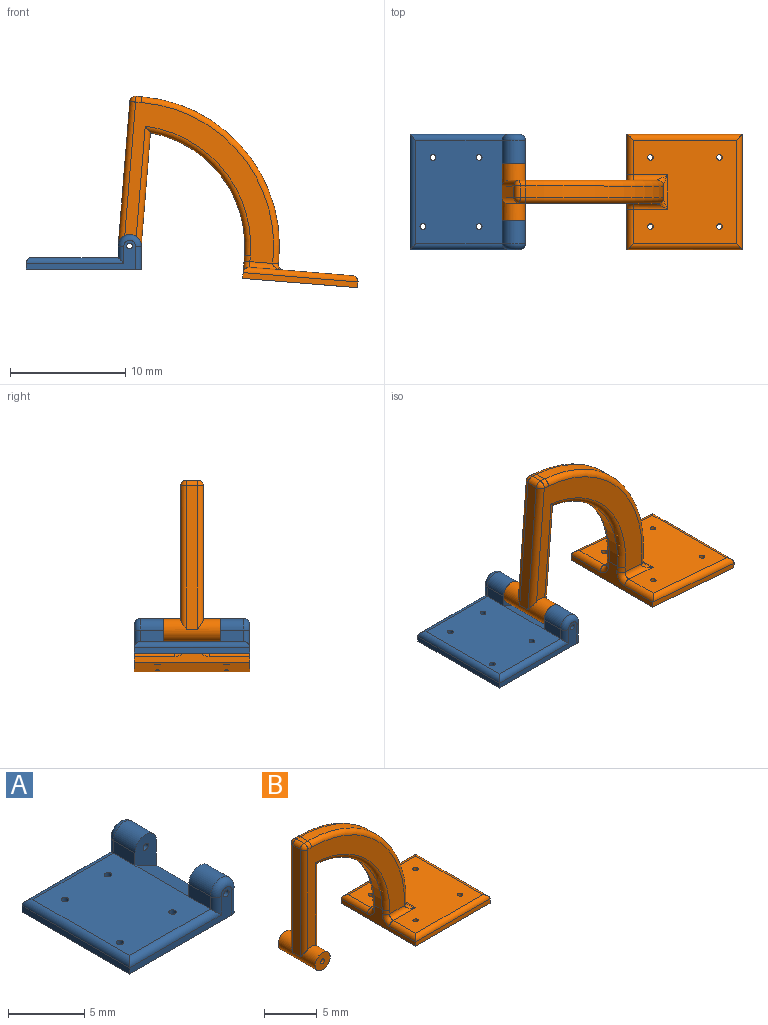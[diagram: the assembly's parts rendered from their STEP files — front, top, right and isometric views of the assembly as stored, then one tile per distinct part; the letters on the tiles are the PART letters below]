
ASSEMBLY  parts=2 mates=1
PART A: 29 faces, bbox 10.1x10x3.1 mm
  f0: plane 2x2mm, normal (1,0,0), area 4mm2, adj f2,f9,f18,f28
  f1: plane 2x1mm, normal (-1,0,0), area 2mm2, adj f5,f7,f19,f23
  f2: cylinder r=1mm len=2mm, axis (0,1,0), area 6.3mm2, adj f0,f6,f18,f27
  f3: cylinder r=0.25mm len=2.5mm, axis (0,-1,0), area 3.9mm2, adj f11,f18
  f4: plane 2x2mm, normal (1,0,0), area 4mm2, adj f5,f9,f19,f25
  f5: cylinder r=1mm len=2mm, axis (0,1,0), area 6.3mm2, adj f1,f4,f19,f24
  f6: plane 2x1mm, normal (-1,0,0), area 2mm2, adj f2,f7,f18,f26
  f7: plane 9x7.5mm, normal (0,0,1), area 66.7mm2, adj f1,f6,f12,f13,f14,f15,f17,f20
  f8: plane 10x0.5mm, normal (-1,0,0), area 5mm2, adj f9,f10,f11,f22
  f9: plane 10x10mm, normal (0,0,-1), area 99.1mm2, adj f0,f4,f8,f10,f11,f12,f13,f14
  f10: plane 9.5x2.5mm, normal (0,-1,0), area 6.4mm2, adj f8,f9,f16,f20,f23,f24,f25
  f11: plane 9.5x2.5mm, normal (0,1,0), area 6.4mm2, adj f3,f8,f9,f21,f26,f27,f28
  f12: cylinder r=0.25mm len=1mm, axis (0,0,1), area 1.6mm2, adj f7,f9
  f13: cylinder r=0.25mm len=1mm, axis (0,0,1), area 1.6mm2, adj f7,f9
  f14: cylinder r=0.25mm len=1mm, axis (0,0,1), area 1.6mm2, adj f7,f9
  f15: cylinder r=0.25mm len=1mm, axis (0,0,1), area 1.6mm2, adj f7,f9
  f16: cylinder r=0.25mm len=2.5mm, axis (0,-1,0), area 3.9mm2, adj f10,f19
  f17: plane 5x2mm, normal (0.45,0,0.89), area 11.2mm2, adj f7,f9,f18,f19
  f18: plane 3x2mm, normal (0,-1,0), area 4.4mm2, adj f0,f2,f3,f6,f17
  f19: plane 3x2mm, normal (0,1,0), area 4.4mm2, adj f1,f4,f5,f16,f17
  f20: cylinder r=0.5mm len=8.5mm, axis (1,0,0), area 6.3mm2, adj f7,f10,f22,f23
  f21: cylinder r=0.5mm len=8.5mm, axis (-1,0,0), area 6.3mm2, adj f7,f11,f22,f26
  f22: cylinder r=0.5mm len=10mm, axis (0,-1,0), area 7.6mm2, adj f7,f8,f20,f21
  f23: cylinder r=0.5mm len=1.5mm, axis (0,0,1), area 0.9mm2, adj f1,f10,f20,f24
  f24: torus R=0.5mm, axis (0,-1,0), area 2mm2, adj f5,f10,f23,f25
  f25: cylinder r=0.5mm len=2mm, axis (0,0,-1), area 1.6mm2, adj f4,f9,f10,f24
  f26: cylinder r=0.5mm len=1.5mm, axis (0,0,-1), area 0.9mm2, adj f6,f11,f21,f27
  f27: torus R=0.5mm, axis (0,-1,0), area 2mm2, adj f2,f11,f26,f28
  f28: cylinder r=0.5mm len=2mm, axis (0,0,1), area 1.6mm2, adj f0,f9,f11,f27
PART B: 50 faces, bbox 21x10x16.1 mm
  f0: plane 9x9mm, normal (0,0,1), area 71.2mm2, adj f17,f19,f21,f22,f23,f24,f25,f26
  f1: plane 10x2mm, normal (-1,0,0), area 6.9mm2, adj f2,f4,f5,f8,f17,f18,f20,f25
  f2: plane 10x10mm, normal (0,0,-1), area 99.2mm2, adj f1,f3,f4,f5,f46,f47,f48,f49
  f3: plane 10x0.5mm, normal (1,0,0), area 5mm2, adj f2,f4,f5,f21
  f4: plane 10x0.5mm, normal (0,-1,0), area 5mm2, adj f1,f2,f3,f19
  f5: plane 10x0.5mm, normal (0,1,0), area 5mm2, adj f1,f2,f3,f23
  f6: plane 12.5x1mm, normal (-1,0,0), area 12.5mm2, adj f13,f34,f36,f37
  f7: plane 9.95x1mm, normal (1,0,0), area 9.9mm2, adj f8,f13,f43,f44
  f8: cylinder r=10mm len=9.95mm, axis (0,1,0), area 14.7mm2, adj f1,f7,f16,f29
  f9: cylinder r=13mm len=13.48mm, axis (0,1,0), area 20.9mm2, adj f10,f24,f32,f40
  f10: plane 1x0.5mm, normal (0,0,1), area 0.5mm2, adj f9,f33,f36,f39
  f11: plane 13x13mm, normal (0,-1,0), area 47.7mm2, adj f13,f16,f18,f22,f31,f32,f33,f34
  f12: plane 13x13mm, normal (0,1,0), area 47.7mm2, adj f13,f26,f28,f29,f37,f39,f40,f41
  f13: cylinder r=1mm len=5mm, axis (0,1,0), area 25.9mm2, adj f6,f7,f11,f12,f14,f15,f34,f37
  f14: plane 2x2mm, normal (0,-1,0), area 2.9mm2, adj f13,f45
  f15: plane 2x2mm, normal (0,1,0), area 2.9mm2, adj f13,f45
  f16: torus R=10.5mm, axis (0,-1,0), area 11.9mm2, adj f8,f11,f18,f44
  f17: cylinder r=0.5mm len=3.5mm, axis (0,1,0), area 2.6mm2, adj f0,f1,f19,f20
  f18: cylinder r=0.5mm len=0.5mm, axis (0,0,1), area 0.4mm2, adj f1,f11,f16,f20
  f19: cylinder r=0.5mm len=10mm, axis (1,0,0), area 7.6mm2, adj f0,f4,f17,f21
  f20: torus R=1mm, axis (-1,0,0), area 0.8mm2, adj f1,f17,f18,f22
  f21: cylinder r=0.5mm len=10mm, axis (0,-1,0), area 7.6mm2, adj f0,f3,f19,f23
  f22: cylinder r=0.5mm len=2.99mm, axis (-1,0,0), area 1.8mm2, adj f0,f11,f20,f30
  f23: cylinder r=0.5mm len=10mm, axis (-1,0,0), area 7.6mm2, adj f0,f5,f21,f25
  f24: cylinder r=0.5mm len=3mm, axis (0,1,0), area 1.4mm2, adj f0,f9,f30,f31,f41,f42
  f25: cylinder r=0.5mm len=3.5mm, axis (0,1,0), area 2.6mm2, adj f0,f1,f23,f27
  f26: cylinder r=0.5mm len=2.99mm, axis (1,0,0), area 1.8mm2, adj f0,f12,f27,f42
  f27: torus R=1mm, axis (-1,0,0), area 0.8mm2, adj f1,f25,f26,f28
  f28: cylinder r=0.5mm len=0.5mm, axis (0,0,-1), area 0.4mm2, adj f1,f12,f27,f29
  f29: torus R=10.5mm, axis (0,-1,0), area 11.9mm2, adj f8,f12,f28,f43
  f30: bspline ~1x1mm, area 0.5mm2, adj f22,f24,f31
  f31: torus R=1mm, axis (0,-1,0), area 0mm2, adj f11,f24,f30,f32
  f32: torus R=12.5mm, axis (0,-1,0), area 16.2mm2, adj f9,f11,f31,f33
  f33: cylinder r=0.5mm len=0.5mm, axis (1,0,0), area 0.4mm2, adj f10,f11,f32,f35
  f34: cylinder r=0.5mm len=12.5mm, axis (0,0,1), area 9.4mm2, adj f6,f11,f13,f35
  f35: sphere r=0.5mm, area 0.4mm2, adj f33,f34,f36
  f36: cylinder r=0.5mm len=1mm, axis (0,1,0), area 0.8mm2, adj f6,f10,f35,f38
  f37: cylinder r=0.5mm len=12.5mm, axis (0,0,-1), area 9.4mm2, adj f6,f12,f13,f38
  f38: sphere r=0.5mm, area 0.4mm2, adj f36,f37,f39
  f39: cylinder r=0.5mm len=0.5mm, axis (-1,0,0), area 0.4mm2, adj f10,f12,f38,f40
  f40: torus R=12.5mm, axis (0,-1,0), area 16.2mm2, adj f9,f12,f39,f41
  f41: torus R=1mm, axis (0,-1,0), area 0mm2, adj f12,f24,f40,f42
  f42: bspline ~1x1mm, area 0.5mm2, adj f24,f26,f41
  f43: cylinder r=0.5mm len=10.49mm, axis (0,0,1), area 7.6mm2, adj f7,f12,f13,f29
  f44: cylinder r=0.5mm len=10.49mm, axis (0,0,-1), area 7.6mm2, adj f7,f11,f13,f16
  f45: cylinder r=0.25mm len=5mm, axis (0,-1,0), area 7.9mm2, adj f14,f15
  f46: cylinder r=0.25mm len=1mm, axis (0,0,1), area 1.6mm2, adj f0,f2
  f47: cylinder r=0.25mm len=1mm, axis (0,0,1), area 1.6mm2, adj f0,f2
  f48: cylinder r=0.25mm len=1mm, axis (0,0,1), area 1.6mm2, adj f0,f2
  f49: cylinder r=0.25mm len=1mm, axis (0,0,1), area 1.6mm2, adj f0,f2
PLACE A at identity fixed
PLACE B rot(axis=(0,1,0),4.6deg) t=(-1.16,-5,0.01)mm
MATE revolute B.f8 <-> A.f2  axis (0,1,0) through (-1,-7.5,2)mm
